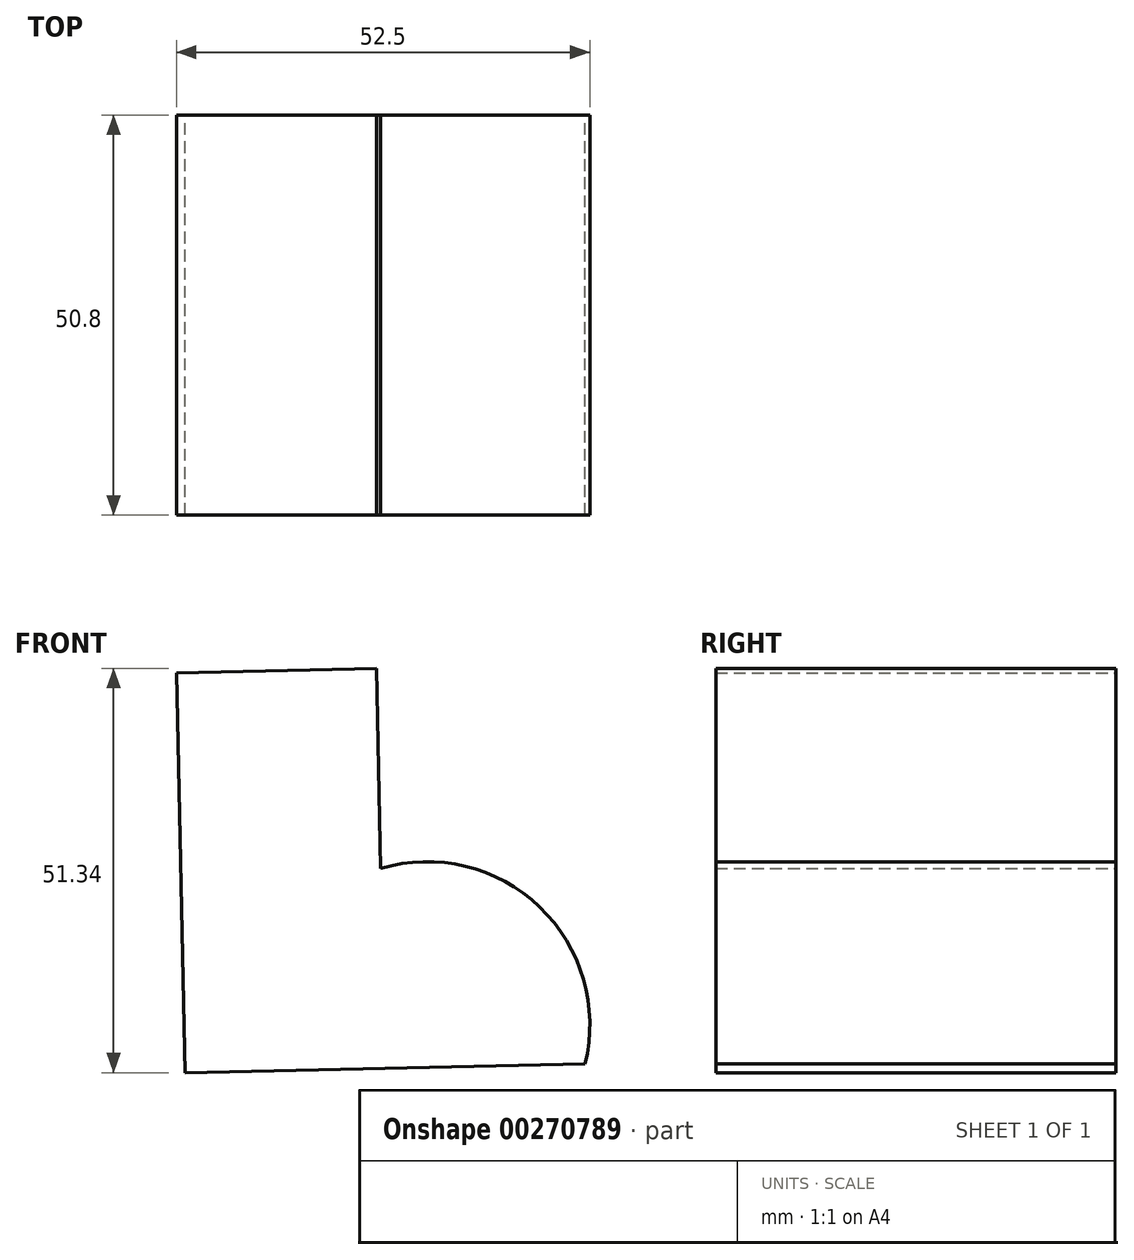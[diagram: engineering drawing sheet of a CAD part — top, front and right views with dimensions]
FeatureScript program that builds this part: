
annotation { "Feature Type Name" : "Feature", "Feature Type Description" : "" }
export const myFeature = defineFeature(function(context is Context, id is Id, definition is map)
    precondition{}
    {
        {
            var Q0;
            Q0=qCreatedBy(makeId("Front.planeOp"),FACE);
            var sketch = newSketch(context, id + "F0", { "sketchPlane" : qUnion([Q0])});
            skLineSegment(sketch, "E0", {"start": v(-50.98, 33.8) * mm, "end": v(-49.88, -16.99) * mm});
            skLineSegment(sketch, "E1", {"start": v(-49.88, -16.99) * mm, "end": v(0.9, -15.88) * mm});
            skLineSegment(sketch, "E2", {"start": v(-50.98, 33.8) * mm, "end": v(-25.6, 34.35) * mm});
            skLineSegment(sketch, "E3", {"start": v(-25.6, 34.35) * mm, "end": v(-25.04, 8.96) * mm});
            skArc(sketch, "E4", {"start": v(0.9, -15.88) * mm, "mid": v(-4.86, 4.07) * mm, "end": v(-25.04, 8.96) * mm});
            skSolve(sketch);
        }
        {
            var Q0;
            Q0 = qSketchRegion(id + "F0", true);
            extrude(context, id + "F1", {"entities" : qUnion([Q0]), "depth" : 50.8 * mm});
        }
    });
